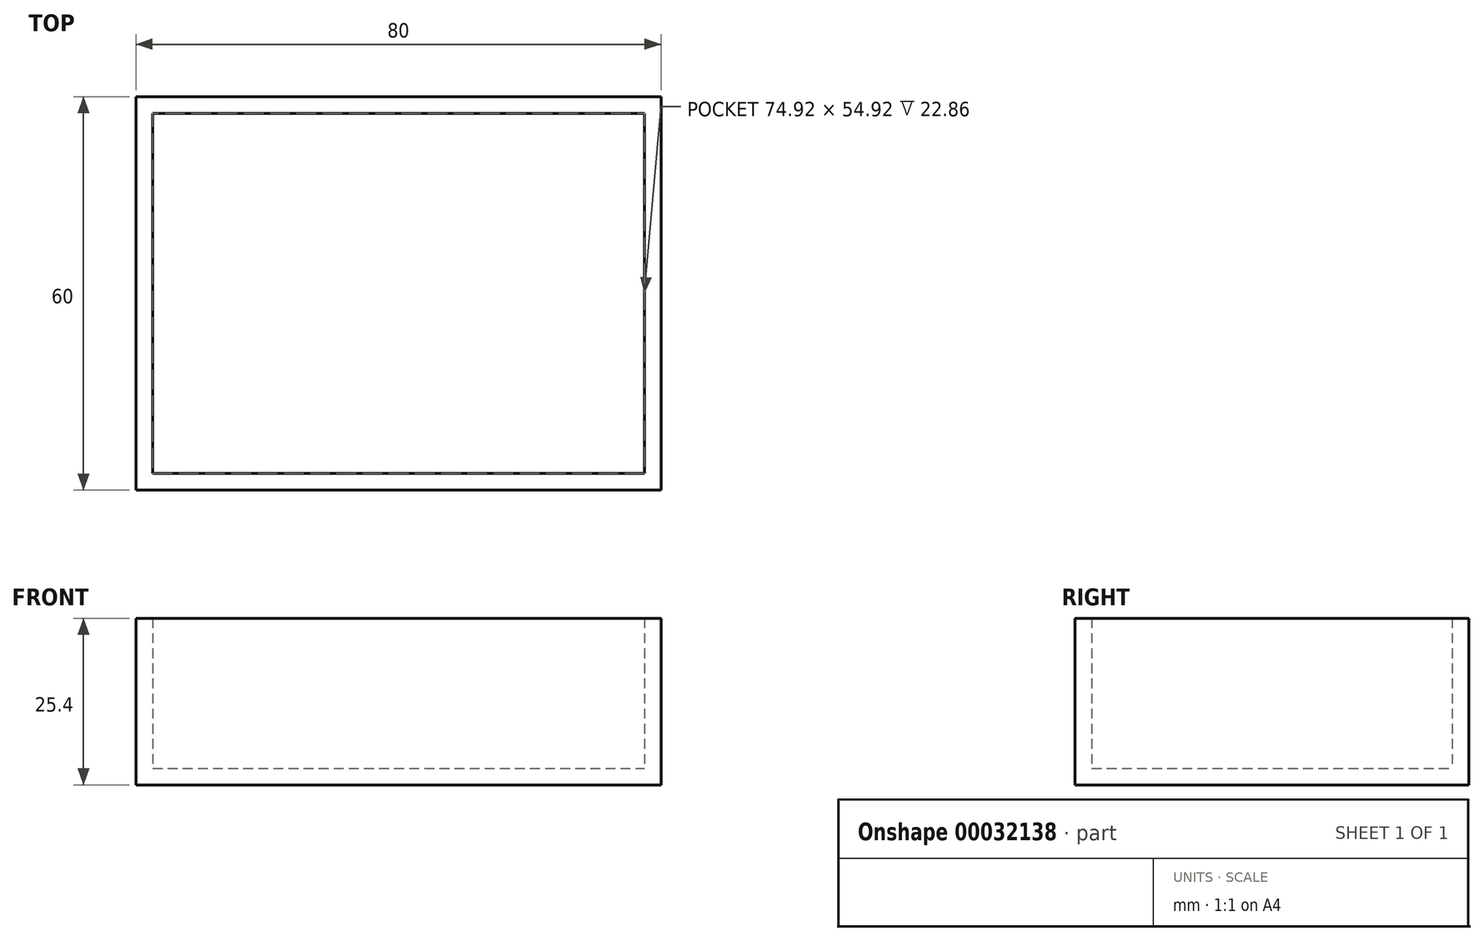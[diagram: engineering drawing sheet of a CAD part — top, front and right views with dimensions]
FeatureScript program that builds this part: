
annotation { "Feature Type Name" : "Feature", "Feature Type Description" : "" }
export const myFeature = defineFeature(function(context is Context, id is Id, definition is map)
    precondition{}
    {
        {
            var Q0;
            Q0=qCreatedBy(makeId("Top.planeOp"),FACE);
            var sketch = newSketch(context, id + "F0", { "sketchPlane" : qUnion([Q0])});
            skLineSegment(sketch, "E0.bottom", {"start": v(0, 0) * mm, "end": v(80, 0) * mm});
            skLineSegment(sketch, "E0.top", {"start": v(0, 60) * mm, "end": v(80, 60) * mm});
            skLineSegment(sketch, "E0.left", {"start": v(0, 0) * mm, "end": v(0, 60) * mm});
            skLineSegment(sketch, "E0.right", {"start": v(80, 0) * mm, "end": v(80, 60) * mm});
            skSolve(sketch);
        }
        {
            var Q0;
            Q0=makeQuery(id+"F0.imprint","IMPRINT",FACE,{"disambiguationData":[TD([[makeQuery(id+"F0.imprint","IMPRINT",EDGE,{"derivedFrom":sQuery(id+"F0.wireOp",EDGE,"E0.bottom")}),1.0]])]});
            extrude(context, id + "F1", {"entities" : qUnion([Q0]), "depth" : 25.4 * mm});
        }
        {
            var Q0;
            Q0=makeQuery(id+"F1.opExtrude","CAP_FACE",FACE,{"disambiguationData":[OSD([sQuery(id+"F0.wireOp",EDGE,"E0.bottom"),sQuery(id+"F0.wireOp",EDGE,"E0.top"),sQuery(id+"F0.wireOp",EDGE,"E0.left"),sQuery(id+"F0.wireOp",EDGE,"E0.right")])],"isStart":false});
            shell(context, id + "F2", {"entities" : qUnion([Q0]), "thickness" : 2.54 * mm});
        }
    });
